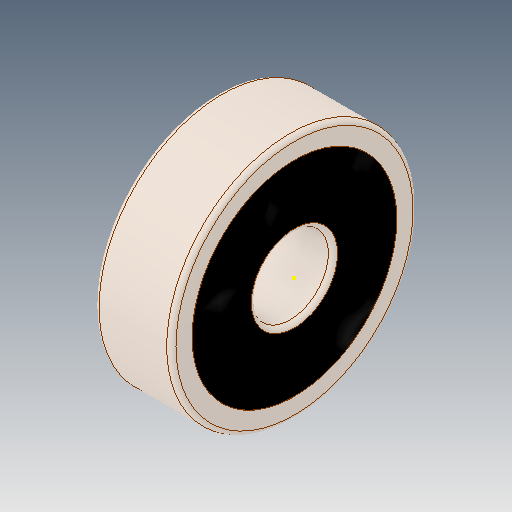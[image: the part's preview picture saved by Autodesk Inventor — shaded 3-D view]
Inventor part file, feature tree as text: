
AUTODESK INVENTOR PART (.ipt)
format: ipt  version: 2017 (Build 210142000, 142)  size: 2,076,160 bytes
history: mixed  units: mm
features: other x20, sketch x3, extrude x2, imported_body x1
ambient origin geometry x8: Origin, YZ Plane, XZ Plane, XY Plane, X Axis, Y Axis, Z Axis, Center Point
bodies: Solid1 (imported_parasolid), Solid2 (imported_parasolid), Solid3 (imported_parasolid), Solid4 (imported_parasolid), Solid5 (imported_parasolid), Solid6 (imported_parasolid), Solid7 (imported_parasolid), Solid8 (imported_parasolid), Solid9 (imported_parasolid), Solid10 (imported_parasolid), Solid11 (imported_parasolid), Solid12 (imported_parasolid), Solid13 (imported_parasolid), Solid14 (imported_parasolid), Solid15 (imported_parasolid), Solid16 (imported_parasolid), Solid17 (imported_parasolid), Solid18 (imported_parasolid), Solid19 (imported_parasolid), Solid20 (imported_parasolid)
feature tree (26):
  extrude  "Extrusion1"  Depth=0.5mm TaperAngle=0.0deg
  extrude  "Extrusion2"  [1 undecoded]
  sketch  "Sketch3"
  sketch  "Sketch1"  dims[d0=0.5mm d1=0.0mm d2=0.5mm d3=0.0mm]
  sketch  "Sketch2"
  other  "SKF 625 Inner Race^SKF 625:1"
  other  "SKF 625 Outer Race^SKF 625:1"
  other  "SKF 625 Ball^SKF 625:1"
  other  "SKF 625 Ball^SKF 625:2"
  other  "SKF 625 Ball^SKF 625:3"
  other  "SKF 625 Ball^SKF 625:4"
  other  "SKF 625 Ball^SKF 625:5"
  other  "SKF 625 Ball^SKF 625:6"
  other  "SKF 625 Ball^SKF 625:7"
  other  "SKF 625 Ball^SKF 625:8"
  other  "SKF 625 Cage^SKF 625:1"
  other  "SKF 625 Cage^SKF 625:2"
  other  "SKF 625 Cage^SKF 625:3"
  other  "SKF 625 Cage^SKF 625:4"
  other  "SKF 625 Cage^SKF 625:5"
  other  "SKF 625 Cage^SKF 625:6"
  other  "SKF 625 Cage^SKF 625:7"
  other  "SKF 625 Cage^SKF 625:8"
  other  "SKF 625 Cage^SKF 625:9"
  other  "SKF 625 Cage^SKF 625:10"
  imported_body  NMx_Import_Brep_tag  [imported B-rep: ~49 faces, bbox_mm=[0.0, 10.2, 10.2]]
note: 1 required parameter value undecoded (feature->parameter linkage not recoverable at this tier; creation-order binding heuristic only, values carry confidence <= 0.55)
